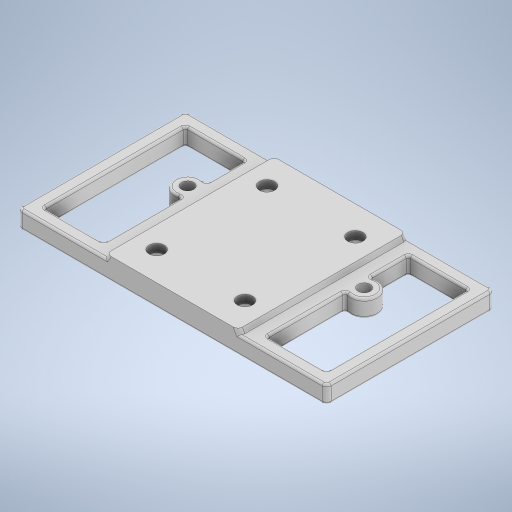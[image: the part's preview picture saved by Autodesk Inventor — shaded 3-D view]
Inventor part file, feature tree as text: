
AUTODESK INVENTOR PART (.ipt)
format: ipt  version: 2024.2 (Build 282272000, 272)  size: 455,680 bytes
history: native  units: mm
features: sketch x7, extrude x5, fillet x3, chamfer x2, hole x2
ambient origin geometry x8: Origin, YZ Plane, XZ Plane, XY Plane, X Axis, Y Axis, Z Axis, Center Point
bodies: Solid1 (feature_tree)
feature tree (19):
  extrude  "Extrusion1"  Depth=38.0mm
  extrude  "Extrusion2"  Depth=2.0mm
  chamfer  "Chamfer2"  Distance=1.0mm
  chamfer  "Chamfer3"  Distance=1.0mm Angle=30.0deg
  fillet  "Fillet1"  Radius=1.0mm
  hole  "Hole1"  [1 undecoded]
  extrude  "Extrusion4"  Depth=25.0mm
  hole  "Hole2"  [1 undecoded]
  extrude  "Extrusion5"  Depth=0.2mm
  fillet  "Fillet5"  Radius=2.8mm
  fillet  "Fillet3"  Radius=55.0mm
  extrude  "Extrusion6"  Depth=0.2mm
  sketch  "Sketch1"  dims[d0=70.0mm d1=38.0mm]
  sketch  "Sketch2"  dims[d2=4.0mm d3=0.0mm d4=31.0mm d5=1.0mm d6=0.0mm d10=1.0mm d11=2.0mm d12=30.0deg]
  sketch  "Sketch4"  dims[d13=1.0mm d14=2.0mm d15=30.0deg d16=1.0mm]
  sketch  "Sketch5"  dims[d27=0.5mm d29=3.5mm]
  sketch  "Sketch6"  dims[d30=20.0mm d31=25.0mm]
  sketch  "Sketch9"  dims[d32=45.0mm d33=31.5mm]
  sketch  "Sketch10"  dims[d34=3.5mm d35=6.0mm d36=5.25mm d37=3.0mm d38=90.0deg d39=8.0mm d40=20.594885mm d41=40.0mm d42=2.8mm d43=55.0mm d44=24.0mm d48=4.5mm d49=4.5mm d50=10.0mm d51=0.0mm d52=40.0mm d53=2.8mm d55=55.0mm d56=23.5mm d57=2.8mm d58=6.0mm d59=5.25mm d60=3.0mm d61=90.0deg d62=8.0mm d63=20.594885mm d64=3.0mm d65=3.0mm d66=3.0mm d67=3.0mm d68=3.0mm d69=3.0mm d70=6.0mm d71=0.0mm d72=0.0mm d73=0.5mm d74=0.2mm d75=0.0mm d28=0.0mm]
note: 2 required parameter values undecoded (feature->parameter linkage not recoverable at this tier; creation-order binding heuristic only, values carry confidence <= 0.55)
